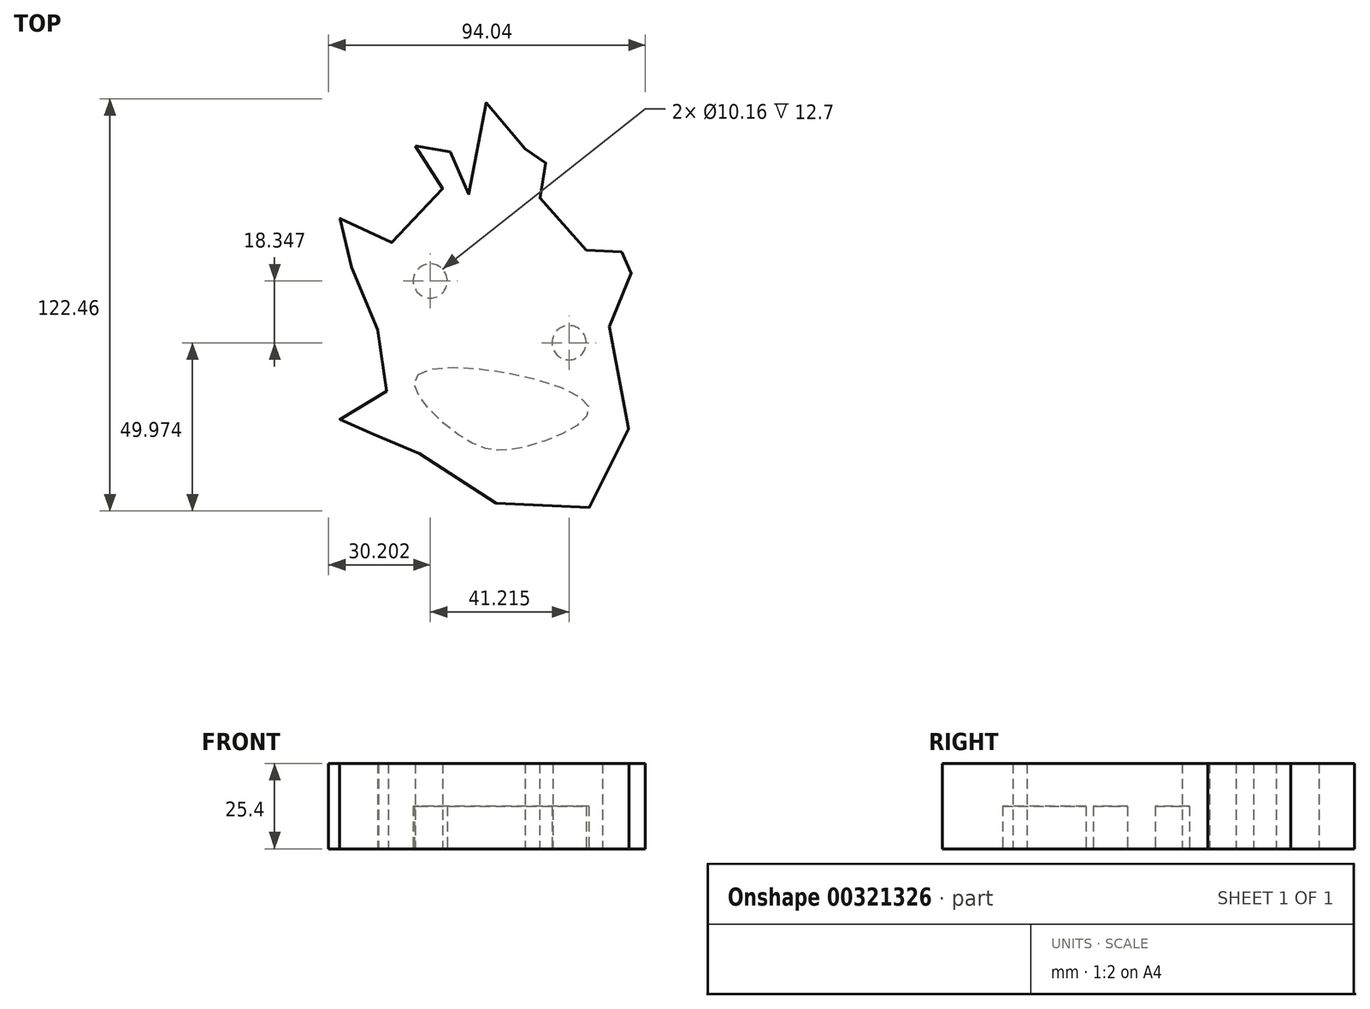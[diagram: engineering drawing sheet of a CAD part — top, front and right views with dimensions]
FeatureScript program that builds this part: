
annotation { "Feature Type Name" : "Feature", "Feature Type Description" : "" }
export const myFeature = defineFeature(function(context is Context, id is Id, definition is map)
    precondition{}
    {
        {
            var Q0;
            Q0=qCreatedBy(makeId("Top.planeOp"),FACE);
            var sketch = newSketch(context, id + "F0", { "sketchPlane" : qUnion([Q0])});
            skFitSpline(sketch, "E0", {"points": [v(-26.02, 49.24) * mm, v(-20.98, 42.8) * mm, v(-18.74, 31.9) * mm, v(-37.2, 20.42) * mm, v(-47.28, 27.98) * mm, v(-51.47, 19.02) * mm, v(-38.6, 8.11) * mm, v(-36.93, -12.3) * mm, v(-34.4, -23.5) * mm, v(-46.16, -28.81) * mm, v(-48.12, -34.69) * mm, v(-42.8, -38.33) * mm, v(-31.33, -34.13) * mm, v(-20.7, -47.84) * mm, v(12.03, -59.03) * mm, v(33.01, -52.6) * mm, v(34.4, -10.63) * mm, v(30.21, 3.36) * mm, v(42.24, 16.5) * mm, v(38.6, 19.58) * mm, v(27.98, 12.03) * mm, v(22.66, 22.66) * mm, v(10.91, 34.13) * mm, v(14.83, 41.96) * mm, v(12.87, 44.2) * mm, v(7.27, 40) * mm, v(5.04, 58.75) * mm, v(-6.15, 60.7) * mm, v(-10.35, 33.3) * mm, v(-14.27, 43.92) * mm, v(-20.7, 52.6) * mm, v(-26.02, 49.24) * mm]});
            skSolve(sketch);
        }
        {
            var Q0;
            Q0 = qSketchRegion(id + "F0", true);
            extrude(context, id + "F1", {"entities" : qUnion([Q0]), "depth" : 25.4 * mm});
        }
        {
            var Q0;
            Q0=qCreatedBy(makeId("Top.planeOp"),FACE);
            var sketch = newSketch(context, id + "F2", { "sketchPlane" : qUnion([Q0])});
            skLineSegment(sketch, "E1", {"start": v(-21.54, 0) * mm, "end": v(-21.54, 9.04) * mm, "construction": true});
            skLineSegment(sketch, "E2", {"start": v(-21.54, 9.04) * mm, "end": v(19.68, -9.3) * mm, "construction": true});
            skCircle(sketch, "E3", {"center": v(-21.54, 9.04) * mm, "radius": 5.08 * mm});
            skCircle(sketch, "E4", {"center": v(19.68, -9.3) * mm, "radius": 5.08 * mm});
            skFitSpline(sketch, "E5", {"points": [v(-25.18, -18.74) * mm, v(25.18, -27.7) * mm, v(7.55, -40) * mm, v(-12.3, -37.2) * mm, v(-25.18, -18.74) * mm]});
            skSolve(sketch);
        }
        {
            var Q0;
            Q0 = qSketchRegion(id + "F2", true);
            extrude(context, id + "F3", {"entities" : qUnion([Q0]), "operationType" : NewBodyOperationType.REMOVE, "depth" : 12.7 * mm});
        }
    });
